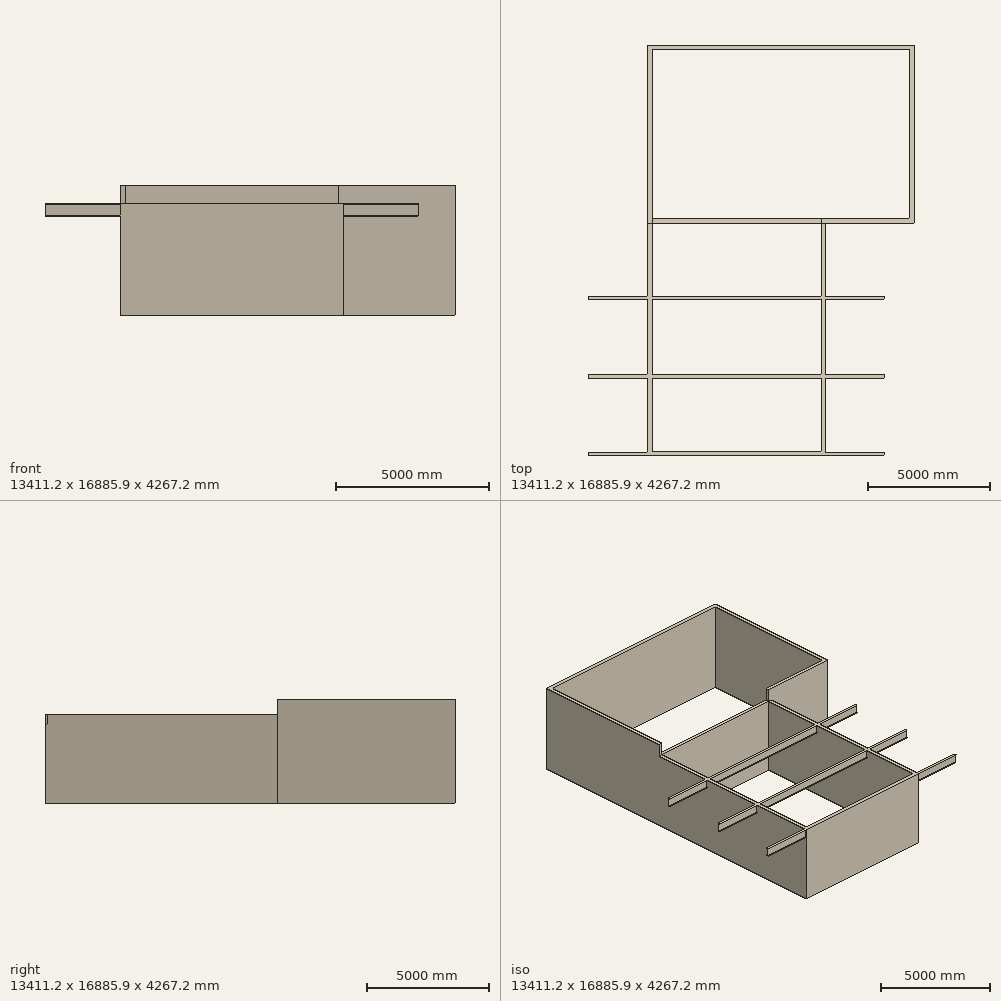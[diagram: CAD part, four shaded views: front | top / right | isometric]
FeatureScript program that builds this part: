
annotation { "Feature Type Name" : "Feature", "Feature Type Description" : "" }
export const myFeature = defineFeature(function(context is Context, id is Id, definition is map)
    precondition{}
    {
        {
            var Q0;
            Q0=qCreatedBy(makeId("Top.planeOp"),FACE);
            var sketch = newSketch(context, id + "F0", { "sketchPlane" : qUnion([Q0])});
            skLineSegment(sketch, "E0", {"start": v(0, 0) * mm, "end": v(0, -9753.6) * mm});
            skLineSegment(sketch, "E1", {"start": v(0, -9753.6) * mm, "end": v(-7315.2, -9753.6) * mm});
            skLineSegment(sketch, "E2", {"start": v(-7315.2, -9753.6) * mm, "end": v(-7315.2, 0) * mm});
            skLineSegment(sketch, "E3", {"start": v(-7315.2, 0) * mm, "end": v(0, 0) * mm});
            skPoint(sketch, "E4.middle", {"position": v(-3657.6, -4876.8) * mm});
            skLineSegment(sketch, "E5", {"start": v(-7132.32, -182.88) * mm, "end": v(-7132.32, -9570.72) * mm});
            skLineSegment(sketch, "E6", {"start": v(-7132.32, -9570.72) * mm, "end": v(-182.88, -9570.72) * mm});
            skLineSegment(sketch, "E7", {"start": v(-182.88, -9570.72) * mm, "end": v(-182.88, -182.88) * mm});
            skLineSegment(sketch, "E8", {"start": v(-7132.32, -182.88) * mm, "end": v(-182.88, -182.88) * mm});
            skSolve(sketch);
        }
        {
            var Q0;
            Q0 = qSketchRegion(id + "F0", true);
            extrude(context, id + "F1", {"entities" : qUnion([Q0]), "depth" : 3657.6 * mm});
        }
        {
            var Q0;
            Q0=makeQuery(id+"F1.opExtrude","CAP_FACE",FACE,{"disambiguationData":[OSD([sQuery(id+"F0.wireOp",EDGE,"E0"),sQuery(id+"F0.wireOp",EDGE,"E1"),sQuery(id+"F0.wireOp",EDGE,"E2"),sQuery(id+"F0.wireOp",EDGE,"E3"),sQuery(id+"F0.wireOp",EDGE,"E5"),sQuery(id+"F0.wireOp",EDGE,"E6"),sQuery(id+"F0.wireOp",EDGE,"E7"),sQuery(id+"F0.wireOp",EDGE,"E8")])],"isStart":false});
            var sketch = newSketch(context, id + "F2", { "sketchPlane" : qUnion([Q0])});
            skLineSegment(sketch, "E9", {"start": v(-7315.2, -182.88) * mm, "end": v(-7315.2, 7132.32) * mm});
            skLineSegment(sketch, "E10", {"start": v(-7315.2, 7132.32) * mm, "end": v(3657.6, 7132.32) * mm});
            skLineSegment(sketch, "E11", {"start": v(3657.6, 7132.32) * mm, "end": v(3657.6, -182.88) * mm});
            skLineSegment(sketch, "E12", {"start": v(3657.6, -182.88) * mm, "end": v(-182.88, -182.88) * mm});
            skLineSegment(sketch, "E13", {"start": v(-182.88, -182.88) * mm, "end": v(-182.88, 0) * mm});
            skLineSegment(sketch, "E14", {"start": v(-182.88, 0) * mm, "end": v(3474.72, 0) * mm});
            skLineSegment(sketch, "E15", {"start": v(3474.72, 0) * mm, "end": v(3474.72, 6949.44) * mm});
            skLineSegment(sketch, "E16", {"start": v(3474.72, 6949.44) * mm, "end": v(-7132.32, 6949.44) * mm});
            skLineSegment(sketch, "E17", {"start": v(-7132.32, 6949.44) * mm, "end": v(-7132.32, -182.88) * mm});
            skLineSegment(sketch, "E18", {"start": v(-7132.32, -182.88) * mm, "end": v(-7315.2, -182.88) * mm});
            skSolve(sketch);
        }
        {
            var Q0;
            Q0 = qSketchRegion(id + "F2", true);
            extrude(context, id + "F3", {"entities" : qUnion([Q0]), "operationType" : NewBodyOperationType.ADD, "oppositeDirection" : true, "depth" : 3657.6 * mm, "hasSecondDirection" : true, "secondDirectionOppositeDirection" : false, "secondDirectionDepth" : 609.6 * mm});
        }
        {
            var Q0;
            Q0=makeQuery(id+"F1.opExtrude","SWEPT_FACE",FACE,{"disambiguationData":[OSD([sQuery(id+"F0.wireOp",EDGE,"E0")])]});
            var sketch = newSketch(context, id + "F4", { "sketchPlane" : qUnion([Q0])});
            skLineSegment(sketch, "E19", {"start": v(-6504.43, 3657.6) * mm, "end": v(-6504.43, 118.9) * mm, "construction": true});
            skLineSegment(sketch, "E20", {"start": v(-3255.26, 3657.6) * mm, "end": v(-3255.26, 194.3) * mm, "construction": true});
            skLineSegment(sketch, "E21", {"start": v(-6504.43, 3657.6) * mm, "end": v(-6574.23, 3657.6) * mm});
            skLineSegment(sketch, "E22", {"start": v(-6574.23, 3657.6) * mm, "end": v(-6574.23, 3644.89) * mm});
            skLineSegment(sketch, "E23", {"start": v(-6574.23, 3644.89) * mm, "end": v(-6507.54, 3644.89) * mm});
            skLineSegment(sketch, "E24", {"start": v(-6507.54, 3644.89) * mm, "end": v(-6507.54, 3454.39) * mm});
            skLineSegment(sketch, "E25", {"start": v(-6501.32, 3454.39) * mm, "end": v(-6501.32, 3644.89) * mm});
            skLineSegment(sketch, "E26", {"start": v(-6501.32, 3644.89) * mm, "end": v(-6434.63, 3644.89) * mm});
            skLineSegment(sketch, "E27", {"start": v(-6434.63, 3644.89) * mm, "end": v(-6434.63, 3657.6) * mm});
            skLineSegment(sketch, "E28", {"start": v(-6434.63, 3657.6) * mm, "end": v(-6504.43, 3657.6) * mm});
            skLineSegment(sketch, "E29", {"start": v(-6507.54, 3454.39) * mm, "end": v(-6501.32, 3454.39) * mm, "construction": true});
            skLineSegment(sketch, "E30.MirrorCS", {"start": v(-6504.43, 3251.18) * mm, "end": v(-6574.23, 3251.18) * mm});
            skLineSegment(sketch, "E31.MirrorCS", {"start": v(-6434.63, 3251.18) * mm, "end": v(-6504.43, 3251.18) * mm});
            skLineSegment(sketch, "E32.MirrorCS", {"start": v(-6434.63, 3263.89) * mm, "end": v(-6434.63, 3251.18) * mm});
            skLineSegment(sketch, "E33.MirrorCS", {"start": v(-6574.23, 3251.18) * mm, "end": v(-6574.23, 3263.89) * mm});
            skLineSegment(sketch, "E34.MirrorCS", {"start": v(-6574.23, 3263.89) * mm, "end": v(-6507.54, 3263.89) * mm});
            skLineSegment(sketch, "E35.MirrorCS", {"start": v(-6501.32, 3263.89) * mm, "end": v(-6434.63, 3263.89) * mm});
            skLineSegment(sketch, "E36.MirrorCS", {"start": v(-6501.32, 3454.39) * mm, "end": v(-6501.32, 3263.89) * mm});
            skLineSegment(sketch, "E37.MirrorCS", {"start": v(-6507.54, 3263.89) * mm, "end": v(-6507.54, 3454.39) * mm});
            skLineSegment(sketch, "E38", {"start": v(-6501.32, 3454.39) * mm, "end": v(-2207.28, 3454.39) * mm, "construction": true});
            skLineSegment(sketch, "E39", {"start": v(-3255.11, 3657.6) * mm, "end": v(-3324.91, 3657.6) * mm});
            skLineSegment(sketch, "E40", {"start": v(-3324.91, 3657.6) * mm, "end": v(-3324.91, 3644.89) * mm});
            skLineSegment(sketch, "E41", {"start": v(-3324.91, 3644.89) * mm, "end": v(-3258.22, 3644.89) * mm});
            skLineSegment(sketch, "E42", {"start": v(-3258.22, 3644.89) * mm, "end": v(-3258.22, 3454.39) * mm});
            skLineSegment(sketch, "E43", {"start": v(-3252, 3454.39) * mm, "end": v(-3252, 3644.89) * mm});
            skLineSegment(sketch, "E44", {"start": v(-3252, 3644.89) * mm, "end": v(-3185.31, 3644.89) * mm});
            skLineSegment(sketch, "E45", {"start": v(-3185.31, 3644.89) * mm, "end": v(-3185.31, 3657.6) * mm});
            skLineSegment(sketch, "E46", {"start": v(-3185.31, 3657.6) * mm, "end": v(-3255.11, 3657.6) * mm});
            skLineSegment(sketch, "E47", {"start": v(-3258.22, 3454.39) * mm, "end": v(-3252, 3454.39) * mm, "construction": true});
            skLineSegment(sketch, "E48.MirrorCS", {"start": v(-3255.11, 3251.18) * mm, "end": v(-3324.91, 3251.18) * mm});
            skLineSegment(sketch, "E49.MirrorCS", {"start": v(-3185.31, 3251.18) * mm, "end": v(-3255.11, 3251.18) * mm});
            skLineSegment(sketch, "E50.MirrorCS", {"start": v(-3185.31, 3263.89) * mm, "end": v(-3185.31, 3251.18) * mm});
            skLineSegment(sketch, "E51.MirrorCS", {"start": v(-3324.91, 3251.18) * mm, "end": v(-3324.91, 3263.89) * mm});
            skLineSegment(sketch, "E52.MirrorCS", {"start": v(-3324.91, 3263.89) * mm, "end": v(-3258.22, 3263.89) * mm});
            skLineSegment(sketch, "E53.MirrorCS", {"start": v(-3252, 3263.89) * mm, "end": v(-3185.31, 3263.89) * mm});
            skLineSegment(sketch, "E54.MirrorCS", {"start": v(-3252, 3454.39) * mm, "end": v(-3252, 3263.89) * mm});
            skLineSegment(sketch, "E55.MirrorCS", {"start": v(-3258.22, 3263.89) * mm, "end": v(-3258.22, 3454.39) * mm});
            skLineSegment(sketch, "E56", {"start": v(-9683.8, 3657.6) * mm, "end": v(-9753.6, 3657.6) * mm});
            skLineSegment(sketch, "E57", {"start": v(-9753.6, 3657.6) * mm, "end": v(-9753.6, 3644.89) * mm});
            skLineSegment(sketch, "E58", {"start": v(-9753.6, 3644.89) * mm, "end": v(-9686.9, 3644.89) * mm});
            skLineSegment(sketch, "E59", {"start": v(-9686.9, 3644.89) * mm, "end": v(-9686.9, 3454.39) * mm});
            skLineSegment(sketch, "E60", {"start": v(-9680.7, 3454.39) * mm, "end": v(-9680.7, 3644.89) * mm});
            skLineSegment(sketch, "E61", {"start": v(-9680.7, 3644.89) * mm, "end": v(-9614, 3644.89) * mm});
            skLineSegment(sketch, "E62", {"start": v(-9614, 3644.89) * mm, "end": v(-9614, 3657.6) * mm});
            skLineSegment(sketch, "E63", {"start": v(-9614, 3657.6) * mm, "end": v(-9683.8, 3657.6) * mm});
            skLineSegment(sketch, "E64", {"start": v(-9686.9, 3454.39) * mm, "end": v(-9680.7, 3454.39) * mm, "construction": true});
            skLineSegment(sketch, "E65.MirrorCS", {"start": v(-9683.8, 3251.18) * mm, "end": v(-9753.6, 3251.18) * mm});
            skLineSegment(sketch, "E66.MirrorCS", {"start": v(-9614, 3251.18) * mm, "end": v(-9683.8, 3251.18) * mm});
            skLineSegment(sketch, "E67.MirrorCS", {"start": v(-9614, 3263.89) * mm, "end": v(-9614, 3251.18) * mm});
            skLineSegment(sketch, "E68.MirrorCS", {"start": v(-9753.6, 3251.18) * mm, "end": v(-9753.6, 3263.89) * mm});
            skLineSegment(sketch, "E69.MirrorCS", {"start": v(-9753.6, 3263.89) * mm, "end": v(-9686.9, 3263.89) * mm});
            skLineSegment(sketch, "E70.MirrorCS", {"start": v(-9680.7, 3263.89) * mm, "end": v(-9614, 3263.89) * mm});
            skLineSegment(sketch, "E71.MirrorCS", {"start": v(-9680.7, 3454.39) * mm, "end": v(-9680.7, 3263.89) * mm});
            skLineSegment(sketch, "E72.MirrorCS", {"start": v(-9686.9, 3263.89) * mm, "end": v(-9686.9, 3454.39) * mm});
            skLineSegment(sketch, "E73", {"start": v(-113.08, 3657.6) * mm, "end": v(-182.88, 3657.6) * mm});
            skLineSegment(sketch, "E74", {"start": v(-182.88, 3657.6) * mm, "end": v(-182.88, 3644.89) * mm});
            skLineSegment(sketch, "E75", {"start": v(-182.88, 3644.89) * mm, "end": v(-116.19, 3644.89) * mm});
            skLineSegment(sketch, "E76", {"start": v(-116.19, 3644.89) * mm, "end": v(-116.19, 3454.39) * mm});
            skLineSegment(sketch, "E77", {"start": v(-109.97, 3454.39) * mm, "end": v(-109.97, 3644.89) * mm});
            skLineSegment(sketch, "E78", {"start": v(-109.97, 3644.89) * mm, "end": v(-43.28, 3644.89) * mm});
            skLineSegment(sketch, "E79", {"start": v(-43.28, 3644.89) * mm, "end": v(-43.28, 3657.6) * mm});
            skLineSegment(sketch, "E80", {"start": v(-43.28, 3657.6) * mm, "end": v(-113.08, 3657.6) * mm});
            skLineSegment(sketch, "E81", {"start": v(-116.19, 3454.39) * mm, "end": v(-109.97, 3454.39) * mm, "construction": true});
            skLineSegment(sketch, "E82.MirrorCS", {"start": v(-113.08, 3251.18) * mm, "end": v(-182.88, 3251.18) * mm});
            skLineSegment(sketch, "E83.MirrorCS", {"start": v(-43.28, 3251.18) * mm, "end": v(-113.08, 3251.18) * mm});
            skLineSegment(sketch, "E84.MirrorCS", {"start": v(-43.28, 3263.89) * mm, "end": v(-43.28, 3251.18) * mm});
            skLineSegment(sketch, "E85.MirrorCS", {"start": v(-182.88, 3251.18) * mm, "end": v(-182.88, 3263.89) * mm});
            skLineSegment(sketch, "E86.MirrorCS", {"start": v(-182.88, 3263.89) * mm, "end": v(-116.19, 3263.89) * mm});
            skLineSegment(sketch, "E87.MirrorCS", {"start": v(-109.97, 3263.89) * mm, "end": v(-43.28, 3263.89) * mm});
            skLineSegment(sketch, "E88.MirrorCS", {"start": v(-109.97, 3454.39) * mm, "end": v(-109.97, 3263.89) * mm});
            skLineSegment(sketch, "E89.MirrorCS", {"start": v(-116.19, 3263.89) * mm, "end": v(-116.19, 3454.39) * mm});
            skSolve(sketch);
        }
        {
            var Q0;
            Q0 = qSketchRegion(id + "F4", true);
            extrude(context, id + "F5", {"entities" : qUnion([Q0]), "operationType" : NewBodyOperationType.ADD, "oppositeDirection" : true, "depth" : 9753.6 * mm, "hasSecondDirection" : true, "secondDirectionOppositeDirection" : false, "secondDirectionDepth" : 2438.4 * mm});
        }
    });
